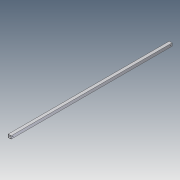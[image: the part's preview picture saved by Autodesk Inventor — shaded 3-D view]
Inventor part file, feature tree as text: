
AUTODESK INVENTOR PART (.ipt)
format: ipt  version: 2012 (Build 160160000, 160)  size: 83,456 bytes
history: native  units: in
note: dims shown in document units (in); Inventor stores cm internally (conversion verified against a paired STEP export)
features: hole x2, extrude x1, sketch x1
ambient origin geometry x8: Origin, YZ Plane, XZ Plane, XY Plane, X Axis, Y Axis, Z Axis, Center Point
bodies: Solid1 (feature_tree)
feature tree (4):
  extrude  "Extrusion1"  Depth=0.125in
  hole  "Hole1"  [1 undecoded]
  hole  "Hole2"  [1 undecoded]
  sketch  "Sketch1"  dims[d0=1.25in d1=0.125in d2=69.0in d3=0.0in d4=0.625in d5=0.75in d6=0.265in d7=0.75in d8=0.375in d9=0.25in d10=0.5635in d11=1.0in d12=0.8108in d13=0.625in d14=0.75in d15=0.265in d16=0.75in d17=0.375in d18=0.25in d19=0.5635in d20=1.0in d21=0.8108in]
note: 2 required parameter values undecoded (feature->parameter linkage not recoverable at this tier; creation-order binding heuristic only, values carry confidence <= 0.55)
